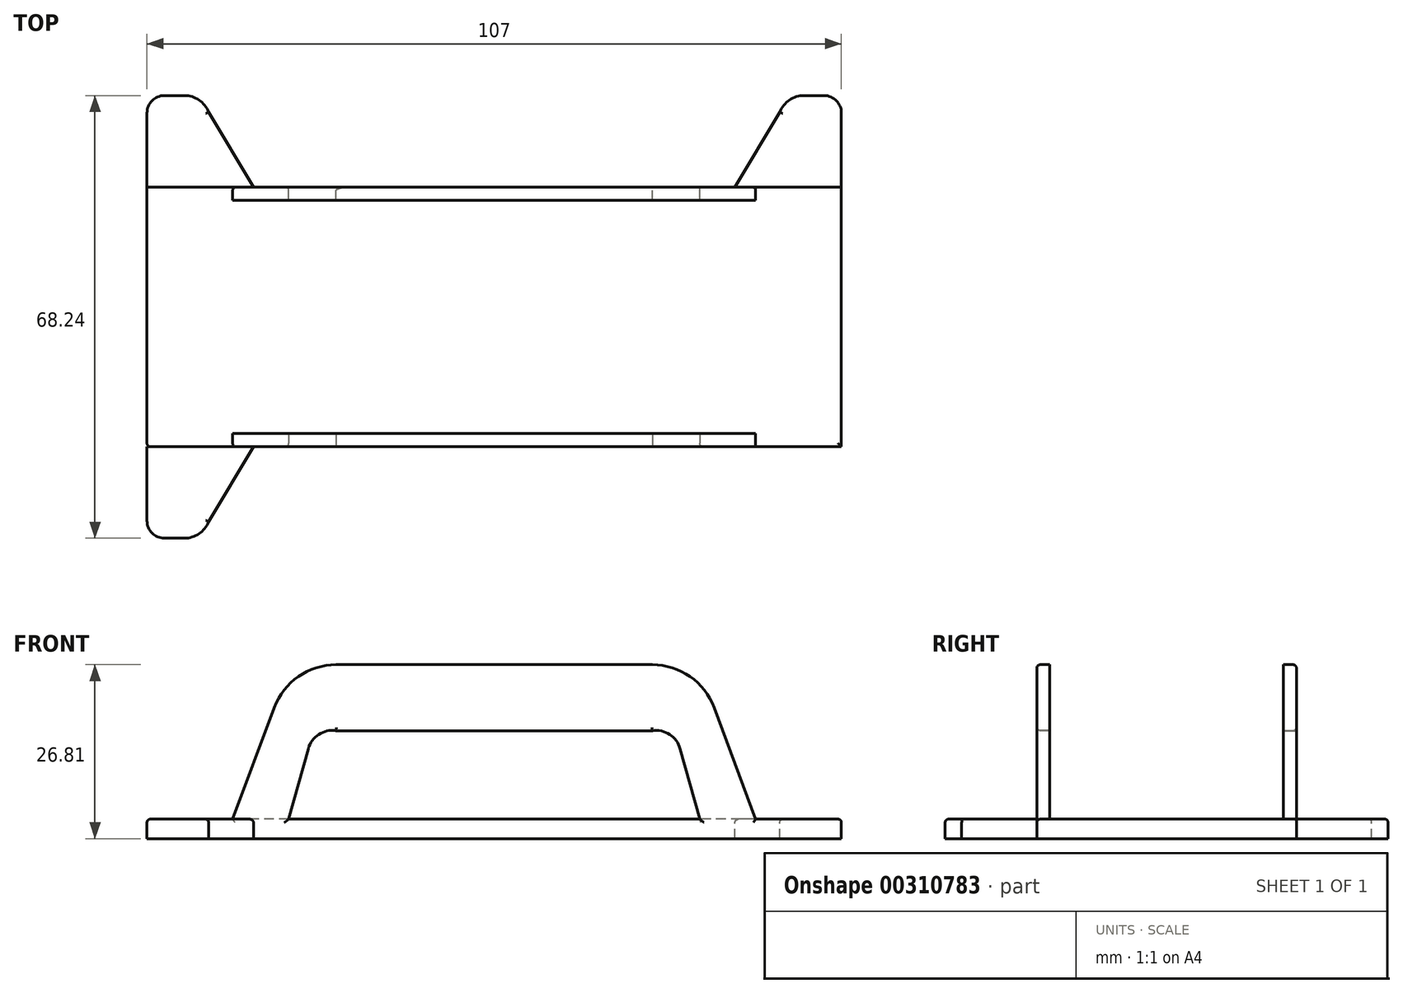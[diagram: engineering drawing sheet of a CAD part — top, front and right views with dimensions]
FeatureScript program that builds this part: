
annotation { "Feature Type Name" : "Feature", "Feature Type Description" : "" }
export const myFeature = defineFeature(function(context is Context, id is Id, definition is map)
    precondition{}
    {
        {
            var Q0;
            Q0=qCreatedBy(makeId("Front.planeOp"),FACE);
            var sketch = newSketch(context, id + "F0", { "sketchPlane" : qUnion([Q0])});
            skLineSegment(sketch, "E0.bottom", {"start": v(53.5, -1.5) * mm, "end": v(-53.5, -1.5) * mm});
            skLineSegment(sketch, "E0.top", {"start": v(53.5, 1.5) * mm, "end": v(-53.5, 1.5) * mm});
            skLineSegment(sketch, "E0.left", {"start": v(53.5, -1.5) * mm, "end": v(53.5, 1.5) * mm});
            skLineSegment(sketch, "E0.right", {"start": v(-53.5, -1.5) * mm, "end": v(-53.5, 1.5) * mm});
            skPoint(sketch, "E0.middle", {"position": v(0, 0) * mm});
            skLineSegment(sketch, "E1", {"start": v(-40.3, 1.5) * mm, "end": v(-33.9, 18.68) * mm});
            skArc(sketch, "E2", {"start": v(-33.9, 18.68) * mm, "mid": v(-30.17, 23.49) * mm, "end": v(-24.36, 25.3) * mm});
            skLineSegment(sketch, "E3", {"start": v(-28.66, 12.34) * mm, "end": v(-31.66, 1.5) * mm});
            skArc(sketch, "E4", {"start": v(-28.66, 12.34) * mm, "mid": v(-27.04, 14.55) * mm, "end": v(-24.36, 15.14) * mm});
            skLineSegment(sketch, "E5", {"start": v(-24.36, 25.3) * mm, "end": v(0, 25.3) * mm});
            skLineSegment(sketch, "E6", {"start": v(-24.36, 15.14) * mm, "end": v(0, 15.14) * mm});
            skArc(sketch, "E7.MirrorCS", {"start": v(28.66, 12.34) * mm, "mid": v(27.04, 14.55) * mm, "end": v(24.36, 15.14) * mm});
            skLineSegment(sketch, "E8.MirrorCS", {"start": v(28.66, 12.34) * mm, "end": v(31.66, 1.5) * mm});
            skLineSegment(sketch, "E9.MirrorCS", {"start": v(40.3, 1.5) * mm, "end": v(33.9, 18.68) * mm});
            skArc(sketch, "E10.MirrorCS", {"start": v(33.9, 18.68) * mm, "mid": v(30.17, 23.49) * mm, "end": v(24.36, 25.3) * mm});
            skLineSegment(sketch, "E11.MirrorCS", {"start": v(24.36, 15.14) * mm, "end": v(0, 15.14) * mm});
            skLineSegment(sketch, "E12.MirrorCS", {"start": v(24.36, 25.3) * mm, "end": v(0, 25.3) * mm});
            skSolve(sketch);
        }
        {
            var Q0;
            {var subQ4=sQuery(id+"F0.wireOp",EDGE,"E1");Q0=makeQuery(id+"F0.imprint","IMPRINT",FACE,{"disambiguationData":[TD([[makeQuery(id+"F0.imprint","IMPRINT",EDGE,{"derivedFrom":subQ4}),-1.0]])]});}
            extrude(context, id + "F1", {"entities" : qUnion([Q0]), "depth" : -2 * mm});
        }
        {
            var Q0;
            Q0=makeQuery(id+"F0.imprint","IMPRINT",FACE,{"disambiguationData":[TD([[makeQuery(id+"F0.imprint","IMPRINT",EDGE,{"derivedFrom":sQuery(id+"F0.wireOp",EDGE,"E0.bottom")}),-1.0]])]});
            extrude(context, id + "F2", {"entities" : qUnion([Q0]), "depth" : -20 * mm});
        }
        {
            var Q0;
            Q0=makeQuery(id+"F1.opExtrude","SWEPT_BODY",BODY,{"disambiguationData":[OSD([sQuery(id+"F0.wireOp",EDGE,"E0.top"),sQuery(id+"F0.wireOp",EDGE,"E1"),sQuery(id+"F0.wireOp",EDGE,"E2"),sQuery(id+"F0.wireOp",EDGE,"E3"),sQuery(id+"F0.wireOp",EDGE,"E4"),sQuery(id+"F0.wireOp",EDGE,"E5"),sQuery(id+"F0.wireOp",EDGE,"E6"),sQuery(id+"F0.wireOp",EDGE,"E7.MirrorCS"),sQuery(id+"F0.wireOp",EDGE,"E8.MirrorCS"),sQuery(id+"F0.wireOp",EDGE,"E9.MirrorCS"),sQuery(id+"F0.wireOp",EDGE,"E10.MirrorCS"),sQuery(id+"F0.wireOp",EDGE,"E11.MirrorCS"),sQuery(id+"F0.wireOp",EDGE,"E12.MirrorCS")])]});
            var Q1;
            Q1=makeQuery(id+"F2.opExtrude","SWEPT_BODY",BODY,{"disambiguationData":[OSD([sQuery(id+"F0.wireOp",EDGE,"E0.bottom"),sQuery(id+"F0.wireOp",EDGE,"E0.top"),sQuery(id+"F0.wireOp",EDGE,"E0.left"),sQuery(id+"F0.wireOp",EDGE,"E0.right")])]});
            var Q2;
            Q2=makeQuery(id+"F2.opExtrude","CAP_FACE",FACE,{"disambiguationData":[OSD([sQuery(id+"F0.wireOp",EDGE,"E0.bottom"),sQuery(id+"F0.wireOp",EDGE,"E0.top"),sQuery(id+"F0.wireOp",EDGE,"E0.left"),sQuery(id+"F0.wireOp",EDGE,"E0.right")])],"isStart":false});
            mirror(context, id + "F3", {"operationType" : NewBodyOperationType.ADD, "entities" : qUnion([Q0, Q1]), "mirrorPlane" : qUnion([Q2])});
        }
        {
            var Q0;
            {var subQ0=makeQuery(id+"F2.opExtrude","SWEPT_FACE",FACE,{"disambiguationData":[OSD([sQuery(id+"F0.wireOp",EDGE,"E0.top")])]});Q0=makeQuery(id+"F3.boolean.opBoolean","MERGE",FACE,{"derivedFrom":[subQ0,makeQuery(id+"F3.opPattern","COPY",FACE,{"derivedFrom":subQ0,"instanceName":"1"})]});}
            var sketch = newSketch(context, id + "F4", { "sketchPlane" : qUnion([Q0])});
            skLineSegment(sketch, "E13", {"start": v(-53.5, 40) * mm, "end": v(-53.5, 51.44) * mm});
            skArc(sketch, "E14", {"start": v(-53.5, 51.44) * mm, "mid": v(-52.72, 53.34) * mm, "end": v(-50.82, 54.12) * mm});
            skLineSegment(sketch, "E15", {"start": v(-50.82, 54.12) * mm, "end": v(-47.75, 54.12) * mm});
            skArc(sketch, "E16", {"start": v(-47.75, 54.12) * mm, "mid": v(-45.49, 53.42) * mm, "end": v(-44.01, 51.58) * mm});
            skLineSegment(sketch, "E17", {"start": v(-44.01, 51.58) * mm, "end": v(-37.1, 40) * mm});
            skLineSegment(sketch, "E18", {"start": v(-53.5, 40) * mm, "end": v(-37.1, 40) * mm});
            skLineSegment(sketch, "E19.MirrorCS", {"start": v(44.01, 51.58) * mm, "end": v(37.1, 40) * mm});
            skLineSegment(sketch, "E20.MirrorCS", {"start": v(53.5, 40) * mm, "end": v(37.1, 40) * mm});
            skLineSegment(sketch, "E21.MirrorCS", {"start": v(53.5, 40) * mm, "end": v(53.5, 51.44) * mm});
            skLineSegment(sketch, "E22.MirrorCS", {"start": v(50.82, 54.12) * mm, "end": v(47.75, 54.12) * mm});
            skArc(sketch, "E23.MirrorCS", {"start": v(53.5, 51.44) * mm, "mid": v(52.72, 53.34) * mm, "end": v(50.82, 54.12) * mm});
            skArc(sketch, "E24.MirrorCS", {"start": v(47.75, 54.12) * mm, "mid": v(45.49, 53.42) * mm, "end": v(44.01, 51.58) * mm});
            skLineSegment(sketch, "E25", {"start": v(-53.5, 20) * mm, "end": v(53.5, 20) * mm});
            skLineSegment(sketch, "E26.MirrorCS", {"start": v(-53.5, 0) * mm, "end": v(-53.5, -11.44) * mm});
            skLineSegment(sketch, "E27.MirrorCS", {"start": v(-44.01, -11.58) * mm, "end": v(-37.1, 0) * mm});
            skLineSegment(sketch, "E28.MirrorCS", {"start": v(-50.82, -14.12) * mm, "end": v(-47.75, -14.12) * mm});
            skArc(sketch, "E29.MirrorCS", {"start": v(-47.75, -14.12) * mm, "mid": v(-45.49, -13.42) * mm, "end": v(-44.01, -11.58) * mm});
            skArc(sketch, "E30.MirrorCS", {"start": v(-53.5, -11.44) * mm, "mid": v(-52.72, -13.34) * mm, "end": v(-50.82, -14.12) * mm});
            skLineSegment(sketch, "E31.MirrorCS", {"start": v(44.01, -11.58) * mm, "end": v(37.1, 0) * mm});
            skLineSegment(sketch, "E32.MirrorCS", {"start": v(-53.5, 0) * mm, "end": v(-37.1, 0) * mm});
            skLineSegment(sketch, "E33.MirrorCS", {"start": v(53.5, 0) * mm, "end": v(37.1, 0) * mm});
            skArc(sketch, "E34.MirrorCS", {"start": v(47.75, -14.12) * mm, "mid": v(45.49, -13.42) * mm, "end": v(44.01, -11.58) * mm});
            skLineSegment(sketch, "E35.MirrorCS", {"start": v(50.82, -14.12) * mm, "end": v(47.75, -14.12) * mm});
            skArc(sketch, "E36.MirrorCS", {"start": v(53.5, -11.44) * mm, "mid": v(52.72, -13.34) * mm, "end": v(50.82, -14.12) * mm});
            skLineSegment(sketch, "E37.MirrorCS", {"start": v(53.5, 0) * mm, "end": v(53.5, -11.44) * mm});
            skSolve(sketch);
        }
        {
            var Q0;
            Q0=makeQuery(id+"F4.imprint","IMPRINT",FACE,{"disambiguationData":[TD([[makeQuery(id+"F4.imprint","IMPRINT",EDGE,{"derivedFrom":sQuery(id+"F4.wireOp",EDGE,"E13")}),-1.0]])]});
            var Q1;
            Q1=makeQuery(id+"F4.imprint","IMPRINT",FACE,{"disambiguationData":[TD([[makeQuery(id+"F4.imprint","IMPRINT",EDGE,{"derivedFrom":sQuery(id+"F4.wireOp",EDGE,"E20.MirrorCS")}),-1.0]])]});
            var Q2;
            Q2=makeQuery(id+"F4.imprint","IMPRINT",FACE,{"disambiguationData":[TD([[makeQuery(id+"F4.imprint","IMPRINT",EDGE,{"derivedFrom":sQuery(id+"F4.wireOp",EDGE,"E31.MirrorCS")}),-1.0]])]});
            var Q3;
            Q3=makeQuery(id+"F4.imprint","IMPRINT",FACE,{"disambiguationData":[TD([[makeQuery(id+"F4.imprint","IMPRINT",EDGE,{"derivedFrom":sQuery(id+"F4.wireOp",EDGE,"E26.MirrorCS")}),1.0]])]});
            extrude(context, id + "F5", {"entities" : qUnion([Q0, Q1, Q2, Q3]), "depth" : -3 * mm});
        }
        {
            var Q0;
            Q0=makeQuery(id+"F5.opExtrude","CAP_EDGE",EDGE,{"disambiguationData":[OSD([sQuery(id+"F4.wireOp",EDGE,"E27.MirrorCS")])],"isStart":true});
            var Q1;
            Q1=makeQuery(id+"F5.opExtrude","CAP_EDGE",EDGE,{"disambiguationData":[OSD([sQuery(id+"F4.wireOp",EDGE,"E29.MirrorCS")])],"isStart":true});
            var Q2;
            Q2=makeQuery(id+"F5.opExtrude","CAP_EDGE",EDGE,{"disambiguationData":[OSD([sQuery(id+"F4.wireOp",EDGE,"E28.MirrorCS")])],"isStart":true});
            var Q3;
            Q3=makeQuery(id+"F5.opExtrude","CAP_EDGE",EDGE,{"disambiguationData":[OSD([sQuery(id+"F4.wireOp",EDGE,"E30.MirrorCS")])],"isStart":true});
            var Q4;
            Q4=makeQuery(id+"F5.opExtrude","CAP_EDGE",EDGE,{"disambiguationData":[OSD([sQuery(id+"F4.wireOp",EDGE,"E26.MirrorCS")])],"isStart":true});
            var Q5;
            {var subQ0=makeQuery(id+"F2.opExtrude","SWEPT_EDGE",EDGE,{"disambiguationData":[OSD([sQuery(id+"F0.wireOp",EDGE,"E0.top"),sQuery(id+"F0.wireOp",EDGE,"E0.right")])]});Q5=makeQuery(id+"F3.boolean.opBoolean","MERGE",EDGE,{"derivedFrom":[subQ0,makeQuery(id+"F3.opPattern","COPY",EDGE,{"derivedFrom":subQ0,"instanceName":"1"})]});}
            fillet(context, id + "F6", {"entities" : qUnion([Q0, Q1, Q2, Q3, Q4, Q5]), "radius" : 0.5 * mm, "tangentPropagation" : true, "allowEdgeOverflow" : false});
        }
        {
            var Q0;
            Q0=makeQuery(id+"F5.opExtrude","CAP_EDGE",EDGE,{"disambiguationData":[OSD([sQuery(id+"F4.wireOp",EDGE,"E13")])],"isStart":true});
            var Q1;
            Q1=makeQuery(id+"F5.opExtrude","CAP_EDGE",EDGE,{"disambiguationData":[OSD([sQuery(id+"F4.wireOp",EDGE,"E14")])],"isStart":true});
            var Q2;
            Q2=makeQuery(id+"F5.opExtrude","CAP_EDGE",EDGE,{"disambiguationData":[OSD([sQuery(id+"F4.wireOp",EDGE,"E15")])],"isStart":true});
            var Q3;
            Q3=makeQuery(id+"F5.opExtrude","CAP_EDGE",EDGE,{"disambiguationData":[OSD([sQuery(id+"F4.wireOp",EDGE,"E16")])],"isStart":true});
            var Q4;
            Q4=makeQuery(id+"F5.opExtrude","CAP_EDGE",EDGE,{"disambiguationData":[OSD([sQuery(id+"F4.wireOp",EDGE,"E17")])],"isStart":true});
            var Q5;
            {var subQ1=sQuery(id+"F0.wireOp",EDGE,"E3");var subQ2=sQuery(id+"F0.wireOp",EDGE,"E0.top");Q5=makeQuery(id+"F3.boolean.opBoolean","SPLIT",EDGE,{"disambiguationData":[TD([makeQuery(id+"F3.opPattern","COPY",FACE,{"derivedFrom":makeQuery(id+"F1.opExtrude","SWEPT_FACE",FACE,{"disambiguationData":[OSD([subQ1])]}),"instanceName":"1"})])],"derivedFrom":makeQuery(id+"F3.opPattern","COPY",EDGE,{"derivedFrom":makeQuery(id+"F2.opExtrude","CAP_EDGE",EDGE,{"disambiguationData":[OSD([subQ2])],"isStart":true}),"instanceName":"1"})});}
            var Q6;
            Q6=makeQuery(id+"F3.opPattern","COPY",EDGE,{"derivedFrom":makeQuery(id+"F1.opExtrude","CAP_EDGE",EDGE,{"disambiguationData":[OSD([sQuery(id+"F0.wireOp",EDGE,"E3")])],"isStart":true}),"instanceName":"1"});
            var Q7;
            Q7=makeQuery(id+"F3.opPattern","COPY",EDGE,{"derivedFrom":makeQuery(id+"F1.opExtrude","CAP_EDGE",EDGE,{"disambiguationData":[OSD([sQuery(id+"F0.wireOp",EDGE,"E1")])],"isStart":true}),"instanceName":"1"});
            var Q8;
            Q8=makeQuery(id+"F5.opExtrude","CAP_EDGE",EDGE,{"disambiguationData":[OSD([sQuery(id+"F4.wireOp",EDGE,"E21.MirrorCS")])],"isStart":true});
            var Q9;
            Q9=makeQuery(id+"F5.opExtrude","CAP_EDGE",EDGE,{"disambiguationData":[OSD([sQuery(id+"F4.wireOp",EDGE,"E23.MirrorCS")])],"isStart":true});
            var Q10;
            Q10=makeQuery(id+"F5.opExtrude","CAP_EDGE",EDGE,{"disambiguationData":[OSD([sQuery(id+"F4.wireOp",EDGE,"E22.MirrorCS")])],"isStart":true});
            var Q11;
            Q11=makeQuery(id+"F5.opExtrude","CAP_EDGE",EDGE,{"disambiguationData":[OSD([sQuery(id+"F4.wireOp",EDGE,"E24.MirrorCS")])],"isStart":true});
            var Q12;
            Q12=makeQuery(id+"F5.opExtrude","CAP_EDGE",EDGE,{"disambiguationData":[OSD([sQuery(id+"F4.wireOp",EDGE,"E19.MirrorCS")])],"isStart":true});
            var Q13;
            {var subQ0=makeQuery(id+"F2.opExtrude","SWEPT_EDGE",EDGE,{"disambiguationData":[OSD([sQuery(id+"F0.wireOp",EDGE,"E0.top"),sQuery(id+"F0.wireOp",EDGE,"E0.left")])]});Q13=makeQuery(id+"F3.boolean.opBoolean","MERGE",EDGE,{"derivedFrom":[subQ0,makeQuery(id+"F3.opPattern","COPY",EDGE,{"derivedFrom":subQ0,"instanceName":"1"})]});}
            var Q14;
            Q14=makeQuery(id+"F5.opExtrude","CAP_EDGE",EDGE,{"disambiguationData":[OSD([sQuery(id+"F4.wireOp",EDGE,"E37.MirrorCS")])],"isStart":true});
            var Q15;
            Q15=makeQuery(id+"F5.opExtrude","CAP_EDGE",EDGE,{"disambiguationData":[OSD([sQuery(id+"F4.wireOp",EDGE,"E31.MirrorCS")])],"isStart":true});
            var Q16;
            Q16=makeQuery(id+"F1.opExtrude","CAP_EDGE",EDGE,{"disambiguationData":[OSD([sQuery(id+"F0.wireOp",EDGE,"E9.MirrorCS")])],"isStart":true});
            var Q17;
            Q17=makeQuery(id+"F1.opExtrude","CAP_EDGE",EDGE,{"disambiguationData":[OSD([sQuery(id+"F0.wireOp",EDGE,"E8.MirrorCS")])],"isStart":true});
            var Q18;
            Q18=makeQuery(id+"F1.opExtrude","CAP_EDGE",EDGE,{"disambiguationData":[OSD([sQuery(id+"F0.wireOp",EDGE,"E7.MirrorCS")])],"isStart":true});
            var Q19;
            Q19=makeQuery(id+"F1.opExtrude","CAP_EDGE",EDGE,{"disambiguationData":[OSD([sQuery(id+"F0.wireOp",EDGE,"E6"),sQuery(id+"F0.wireOp",EDGE,"E11.MirrorCS")])],"isStart":true});
            var Q20;
            Q20=makeQuery(id+"F1.opExtrude","CAP_EDGE",EDGE,{"disambiguationData":[OSD([sQuery(id+"F0.wireOp",EDGE,"E3")])],"isStart":true});
            var Q21;
            Q21=makeQuery(id+"F1.opExtrude","CAP_EDGE",EDGE,{"disambiguationData":[OSD([sQuery(id+"F0.wireOp",EDGE,"E4")])],"isStart":true});
            var Q22;
            Q22=makeQuery(id+"F2.opExtrude","CAP_EDGE",EDGE,{"disambiguationData":[OSD([sQuery(id+"F0.wireOp",EDGE,"E0.top")])],"isStart":true});
            fillet(context, id + "F7", {"entities" : qUnion([Q0, Q1, Q2, Q3, Q4, Q5, Q6, Q7, Q8, Q9, Q10, Q11, Q12, Q13, Q14, Q15, Q16, Q17, Q18, Q19, Q20, Q21, Q22]), "radius" : 0.5 * mm, "tangentPropagation" : true, "allowEdgeOverflow" : false});
        }
        {
            var Q0;
            {var subQ0=makeQuery(id+"F2.opExtrude","SWEPT_FACE",FACE,{"disambiguationData":[OSD([sQuery(id+"F0.wireOp",EDGE,"E0.top")])]});Q0=makeQuery(id+"F3.boolean.opBoolean","MERGE",FACE,{"derivedFrom":[subQ0,makeQuery(id+"F3.opPattern","COPY",FACE,{"derivedFrom":subQ0,"instanceName":"1"})]});}
            var sketch = newSketch(context, id + "F8", { "sketchPlane" : qUnion([Q0])});
            skLineSegment(sketch, "E38", {"start": v(-53, 20.25) * mm, "end": v(-53, 31.73) * mm});
            skLineSegment(sketch, "E39", {"start": v(-53, 20.25) * mm, "end": v(-53, 8.79) * mm});
            skLineSegment(sketch, "E40", {"start": v(-53, 31.73) * mm, "end": v(53, 31.73) * mm});
            skLineSegment(sketch, "E41", {"start": v(-53, 8.79) * mm, "end": v(53, 8.79) * mm});
            skSolve(sketch);
        }
        {
            var Q0;
            Q0=makeQuery(id+"F8.imprint","IMPRINT",FACE,{"disambiguationData":[TD([[makeQuery(id+"F8.imprint","IMPRINT",EDGE,{"derivedFrom":sQuery(id+"F8.wireOp",EDGE,"E38")}),1.0]])]});
            extrude(context, id + "F9", {"entities" : qUnion([Q0]), "operationType" : NewBodyOperationType.ADD, "depth" : -0.1 * mm});
        }
    });
